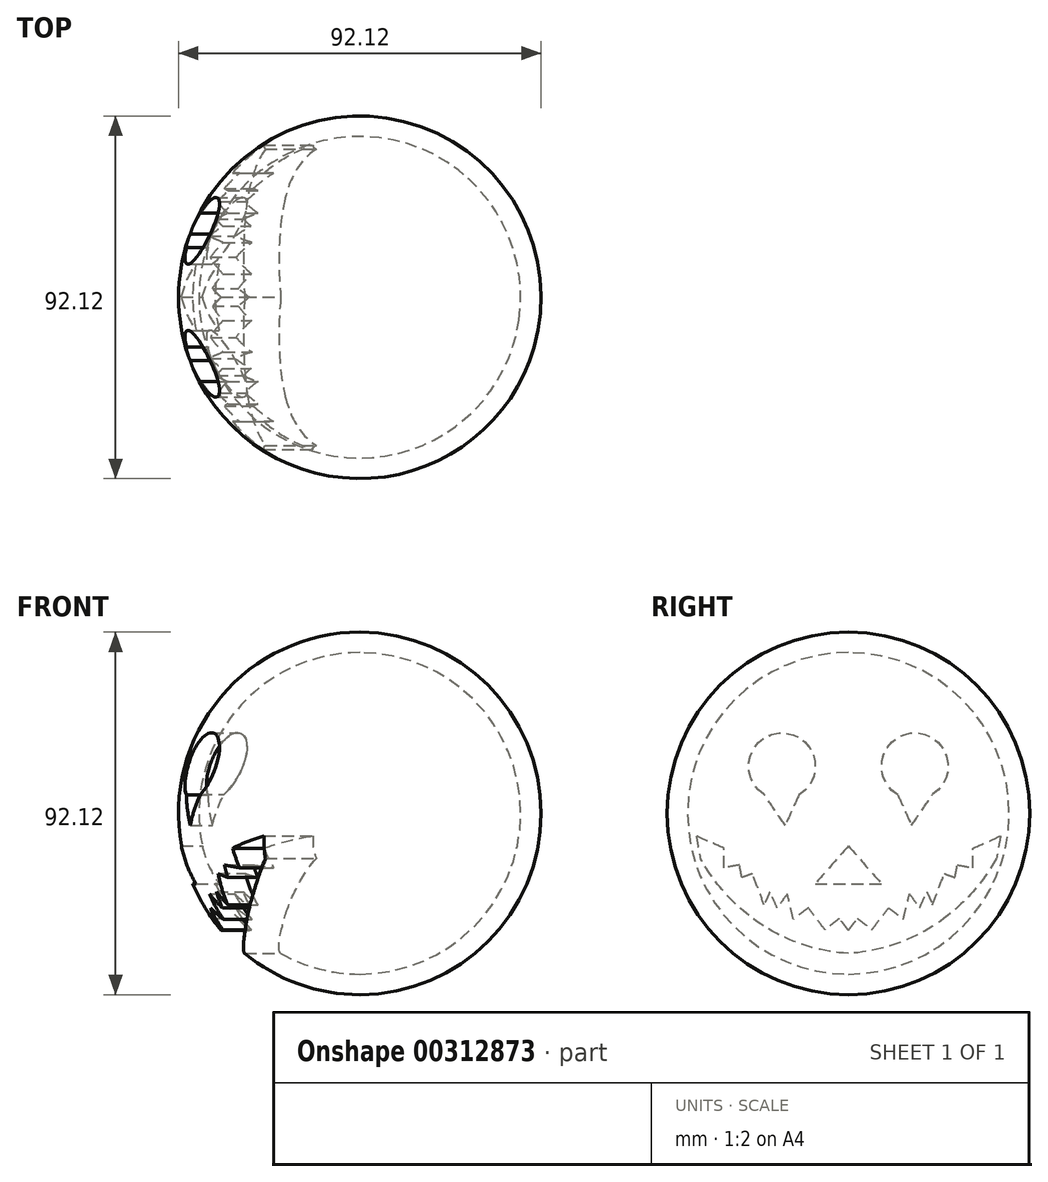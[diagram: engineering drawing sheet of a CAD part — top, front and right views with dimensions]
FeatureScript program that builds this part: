
annotation { "Feature Type Name" : "Feature", "Feature Type Description" : "" }
export const myFeature = defineFeature(function(context is Context, id is Id, definition is map)
    precondition{}
    {
        {
            var Q0;
            Q0=qCreatedBy(makeId("Right.planeOp"),FACE);
            var sketch = newSketch(context, id + "F0", { "sketchPlane" : qUnion([Q0])});
            skArc(sketch, "E0", {"start": v(0, 46.06) * mm, "mid": v(-46.06, 0) * mm, "end": v(0, -46.06) * mm});
            skLineSegment(sketch, "E1", {"start": v(0, 46.06) * mm, "end": v(0, -46.06) * mm});
            skArc(sketch, "E2", {"start": v(0, 40.85) * mm, "mid": v(-40.85, 0) * mm, "end": v(0, -40.85) * mm});
            skSolve(sketch);
        }
        {
            var Q0;
            {var subQ0=sQuery(id+"F0.wireOp",EDGE,"E0");Q0=makeQuery(id+"F0.imprint","IMPRINT",FACE,{"disambiguationData":[TD([[makeQuery(id+"F0.imprint","IMPRINT",EDGE,{"derivedFrom":subQ0}),1.0]])]});}
            var Q1;
            Q1=sQuery(id+"F0.wireOp",EDGE,"E1");
            revolve(context, id + "F1", {"entities" : qUnion([Q0]), "axis" : qUnion([Q1]), "revolveType" : RevolveType.FULL});
        }
        {
            var Q0;
            Q0=qCreatedBy(makeId("Right.planeOp"),FACE);
            var sketch = newSketch(context, id + "F2", { "sketchPlane" : qUnion([Q0])});
            skArc(sketch, "E3", {"start": v(21.41, 4.82) * mm, "mid": v(16.73, 20.46) * mm, "end": v(12.6, 4.66) * mm});
            skLineSegment(sketch, "E4", {"start": v(0, -8.29) * mm, "end": v(8.4, -17.87) * mm});
            skLineSegment(sketch, "E5", {"start": v(8.4, -17.87) * mm, "end": v(0, -17.87) * mm});
            skLineSegment(sketch, "E6", {"start": v(0, -29.68) * mm, "end": v(2.25, -26.73) * mm});
            skLineSegment(sketch, "E7", {"start": v(2.25, -26.73) * mm, "end": v(5.97, -29.56) * mm});
            skLineSegment(sketch, "E8", {"start": v(5.97, -29.56) * mm, "end": v(10.2, -24.02) * mm});
            skArc(sketch, "E9", {"start": v(0, -35.58) * mm, "mid": v(13.36, -32.73) * mm, "end": v(25.22, -25.96) * mm});
            skLineSegment(sketch, "E10", {"start": v(10.2, -24.02) * mm, "end": v(13.96, -26.89) * mm});
            skLineSegment(sketch, "E11", {"start": v(13.96, -26.89) * mm, "end": v(15.51, -20.46) * mm});
            skLineSegment(sketch, "E12", {"start": v(15.51, -20.46) * mm, "end": v(18.1, -24.02) * mm});
            skLineSegment(sketch, "E13", {"start": v(18.1, -24.02) * mm, "end": v(19.94, -19.91) * mm});
            skLineSegment(sketch, "E14", {"start": v(19.94, -19.91) * mm, "end": v(21.41, -23.23) * mm});
            skArc(sketch, "E15", {"start": v(25.22, -25.96) * mm, "mid": v(32.13, -19.3) * mm, "end": v(37.63, -11.44) * mm});
            skPoint(sketch, "E16.start.orphan", {"position": v(25.22, -20.65) * mm});
            skLineSegment(sketch, "E17", {"start": v(21.41, -23.23) * mm, "end": v(24.36, -15.3) * mm});
            skLineSegment(sketch, "E18", {"start": v(24.36, -15.3) * mm, "end": v(27.07, -16.31) * mm});
            skLineSegment(sketch, "E19", {"start": v(27.07, -16.31) * mm, "end": v(27.68, -13.1) * mm});
            skLineSegment(sketch, "E20", {"start": v(27.68, -13.1) * mm, "end": v(31.61, -13.84) * mm});
            skLineSegment(sketch, "E21", {"start": v(31.61, -13.84) * mm, "end": v(31.61, -8.86) * mm});
            skLineSegment(sketch, "E22", {"start": v(31.61, -8.86) * mm, "end": v(34.55, -7.55) * mm});
            skLineSegment(sketch, "E23", {"start": v(34.55, -7.55) * mm, "end": v(38.67, -5.72) * mm});
            skLineSegment(sketch, "E24", {"start": v(38.67, -5.72) * mm, "end": v(37.63, -11.44) * mm});
            skLineSegment(sketch, "E25", {"start": v(12.6, 4.66) * mm, "end": v(16.02, -3.04) * mm});
            skLineSegment(sketch, "E26", {"start": v(16.02, -3.04) * mm, "end": v(21.41, 4.82) * mm});
            skArc(sketch, "E27.MirrorCS", {"start": v(-21.41, 4.82) * mm, "mid": v(-16.73, 20.46) * mm, "end": v(-12.6, 4.66) * mm});
            skLineSegment(sketch, "E28.MirrorCS", {"start": v(-12.6, 4.66) * mm, "end": v(-16.02, -3.04) * mm});
            skLineSegment(sketch, "E29.MirrorCS", {"start": v(-16.02, -3.04) * mm, "end": v(-21.41, 4.82) * mm});
            skLineSegment(sketch, "E30.MirrorCS", {"start": v(0, -8.29) * mm, "end": v(-8.4, -17.87) * mm});
            skLineSegment(sketch, "E31.MirrorCS", {"start": v(-8.4, -17.87) * mm, "end": v(0, -17.87) * mm});
            skArc(sketch, "E32.MirrorCS", {"start": v(0, -35.58) * mm, "mid": v(-13.36, -32.73) * mm, "end": v(-25.22, -25.96) * mm});
            skArc(sketch, "E33.MirrorCS", {"start": v(-25.22, -25.96) * mm, "mid": v(-32.13, -19.3) * mm, "end": v(-37.63, -11.44) * mm});
            skLineSegment(sketch, "E34.MirrorCS", {"start": v(-38.67, -5.72) * mm, "end": v(-37.63, -11.44) * mm});
            skLineSegment(sketch, "E35.MirrorCS", {"start": v(-34.55, -7.55) * mm, "end": v(-38.67, -5.72) * mm});
            skLineSegment(sketch, "E36.MirrorCS", {"start": v(-27.68, -13.1) * mm, "end": v(-31.61, -13.84) * mm});
            skLineSegment(sketch, "E37.MirrorCS", {"start": v(-27.07, -16.31) * mm, "end": v(-27.68, -13.1) * mm});
            skLineSegment(sketch, "E38.MirrorCS", {"start": v(-24.36, -15.3) * mm, "end": v(-27.07, -16.31) * mm});
            skLineSegment(sketch, "E39.MirrorCS", {"start": v(-21.41, -23.23) * mm, "end": v(-24.36, -15.3) * mm});
            skLineSegment(sketch, "E40.MirrorCS", {"start": v(-19.94, -19.91) * mm, "end": v(-21.41, -23.23) * mm});
            skLineSegment(sketch, "E41.MirrorCS", {"start": v(-18.1, -24.02) * mm, "end": v(-19.94, -19.91) * mm});
            skLineSegment(sketch, "E42.MirrorCS", {"start": v(-15.51, -20.46) * mm, "end": v(-18.1, -24.02) * mm});
            skLineSegment(sketch, "E43.MirrorCS", {"start": v(-13.96, -26.89) * mm, "end": v(-15.51, -20.46) * mm});
            skLineSegment(sketch, "E44.MirrorCS", {"start": v(-10.2, -24.02) * mm, "end": v(-13.96, -26.89) * mm});
            skLineSegment(sketch, "E45.MirrorCS", {"start": v(-5.97, -29.56) * mm, "end": v(-10.2, -24.02) * mm});
            skLineSegment(sketch, "E46.MirrorCS", {"start": v(-2.25, -26.73) * mm, "end": v(-5.97, -29.56) * mm});
            skLineSegment(sketch, "E47.MirrorCS", {"start": v(0, -29.68) * mm, "end": v(-2.25, -26.73) * mm});
            skLineSegment(sketch, "E48.MirrorCS", {"start": v(-31.61, -13.84) * mm, "end": v(-31.61, -8.86) * mm});
            skLineSegment(sketch, "E49.MirrorCS", {"start": v(-31.61, -8.86) * mm, "end": v(-34.55, -7.55) * mm});
            skPoint(sketch, "E50.orphan", {"position": v(0, 51.05) * mm});
            skSolve(sketch);
        }
        {
            var Q0;
            Q0 = qSketchRegion(id + "F2", true);
            extrude(context, id + "F3", {"entities" : qUnion([Q0]), "operationType" : NewBodyOperationType.REMOVE, "oppositeDirection" : true, "depth" : 96.77 * mm});
        }
    });
